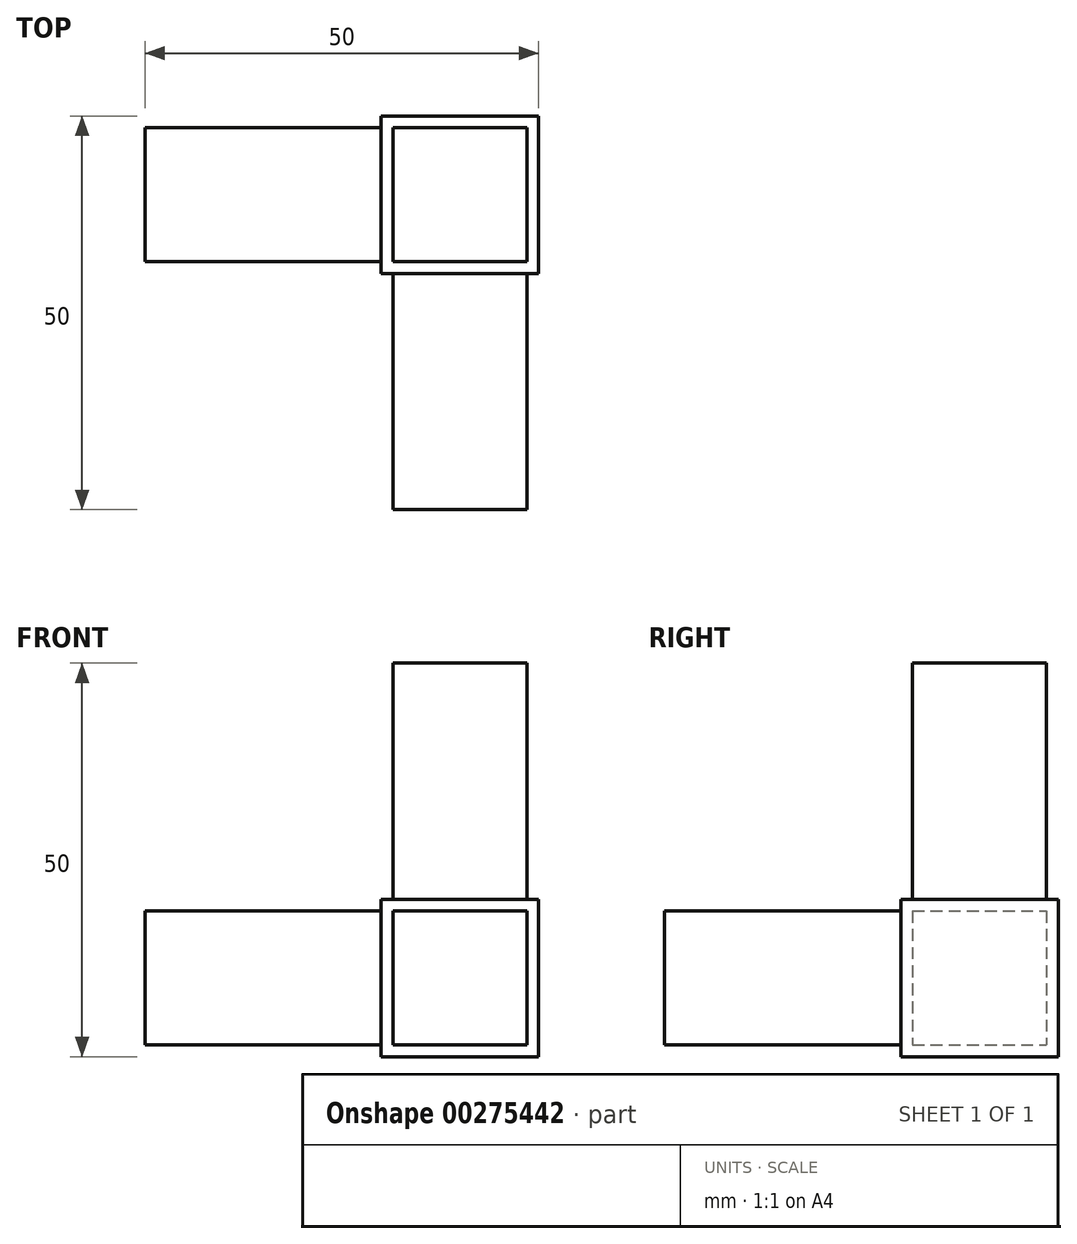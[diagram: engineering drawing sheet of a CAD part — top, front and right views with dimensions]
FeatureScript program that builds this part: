
annotation { "Feature Type Name" : "Feature", "Feature Type Description" : "" }
export const myFeature = defineFeature(function(context is Context, id is Id, definition is map)
    precondition{}
    {
        {
            var Q0;
            Q0=qCreatedBy(makeId("Top.planeOp"),FACE);
            var sketch = newSketch(context, id + "F0", { "sketchPlane" : qUnion([Q0])});
            skLineSegment(sketch, "E0.bottom", {"start": v(10, -10) * mm, "end": v(-10, -10) * mm});
            skLineSegment(sketch, "E0.top", {"start": v(10, 10) * mm, "end": v(-10, 10) * mm});
            skLineSegment(sketch, "E0.left", {"start": v(10, -10) * mm, "end": v(10, 10) * mm});
            skLineSegment(sketch, "E0.right", {"start": v(-10, -10) * mm, "end": v(-10, 10) * mm});
            skPoint(sketch, "E0.middle", {"position": v(0, 0) * mm});
            skLineSegment(sketch, "E1", {"start": v(0, -10) * mm, "end": v(8.5, -10) * mm});
            skLineSegment(sketch, "E2.bottom", {"start": v(8.5, -10) * mm, "end": v(-8.5, -10) * mm});
            skLineSegment(sketch, "E2.top", {"start": v(8.5, -40) * mm, "end": v(-8.5, -40) * mm});
            skLineSegment(sketch, "E2.left", {"start": v(8.5, -10) * mm, "end": v(8.5, -40) * mm});
            skLineSegment(sketch, "E2.right", {"start": v(-8.5, -10) * mm, "end": v(-8.5, -40) * mm});
            skLineSegment(sketch, "E3", {"start": v(-10, 0) * mm, "end": v(-10, -8.5) * mm});
            skLineSegment(sketch, "E4.bottom", {"start": v(-10, -8.5) * mm, "end": v(-40, -8.5) * mm});
            skLineSegment(sketch, "E4.top", {"start": v(-10, 8.5) * mm, "end": v(-40, 8.5) * mm});
            skLineSegment(sketch, "E4.left", {"start": v(-10, -8.5) * mm, "end": v(-10, 8.5) * mm});
            skLineSegment(sketch, "E4.right", {"start": v(-40, -8.5) * mm, "end": v(-40, 8.5) * mm});
            skSolve(sketch);
        }
        {
            var Q0;
            {var subQ1=sQuery(id+"F0.wireOp",EDGE,"E0.top");Q0=makeQuery(id+"F0.imprint","IMPRINT",FACE,{"disambiguationData":[TD([[makeQuery(id+"F0.imprint","IMPRINT",EDGE,{"derivedFrom":subQ1}),1.0]])]});}
            extrude(context, id + "F1", {"entities" : qUnion([Q0]), "depth" : 20 * mm});
        }
        {
            var Q0;
            {var subQ4=sQuery(id+"F0.wireOp",EDGE,"E4.bottom");Q0=makeQuery(id+"F0.imprint","IMPRINT",FACE,{"disambiguationData":[TD([[makeQuery(id+"F0.imprint","IMPRINT",EDGE,{"derivedFrom":subQ4}),-1.0]])]});}
            var Q1;
            Q1=makeQuery(id+"F0.imprint","IMPRINT",FACE,{"disambiguationData":[TD([[makeQuery(id+"F0.imprint","IMPRINT",EDGE,{"derivedFrom":sQuery(id+"F0.wireOp",EDGE,"E2.top")}),-1.0]])]});
            extrude(context, id + "F2", {"entities" : qUnion([Q0, Q1]), "operationType" : NewBodyOperationType.ADD, "depth" : 18.5 * mm, "hasSecondDirection" : true, "secondDirectionOppositeDirection" : false, "secondDirectionDepth" : 1.5 * mm});
        }
        {
            var Q0;
            Q0=makeQuery(id+"F1.opExtrude","CAP_FACE",FACE,{"disambiguationData":[OSD([sQuery(id+"F0.wireOp",EDGE,"E0.bottom"),sQuery(id+"F0.wireOp",EDGE,"E0.top"),sQuery(id+"F0.wireOp",EDGE,"E0.left"),sQuery(id+"F0.wireOp",EDGE,"E0.right"),sQuery(id+"F0.wireOp",EDGE,"E2.bottom"),sQuery(id+"F0.wireOp",EDGE,"E4.left")])],"isStart":false});
            var sketch = newSketch(context, id + "F3", { "sketchPlane" : qUnion([Q0])});
            skLineSegment(sketch, "E5.bottom", {"start": v(8.5, -8.5) * mm, "end": v(-8.5, -8.5) * mm});
            skLineSegment(sketch, "E5.top", {"start": v(8.5, 8.5) * mm, "end": v(-8.5, 8.5) * mm});
            skLineSegment(sketch, "E5.left", {"start": v(8.5, -8.5) * mm, "end": v(8.5, 8.5) * mm});
            skLineSegment(sketch, "E5.right", {"start": v(-8.5, -8.5) * mm, "end": v(-8.5, 8.5) * mm});
            skPoint(sketch, "E5.middle", {"position": v(0, 0) * mm});
            skSolve(sketch);
        }
        {
            var Q0;
            Q0=qSketchRegion(id+"F3",true);
            extrude(context, id + "F4", {"entities" : qUnion([Q0]), "operationType" : NewBodyOperationType.ADD, "depth" : 30 * mm});
        }
    });
